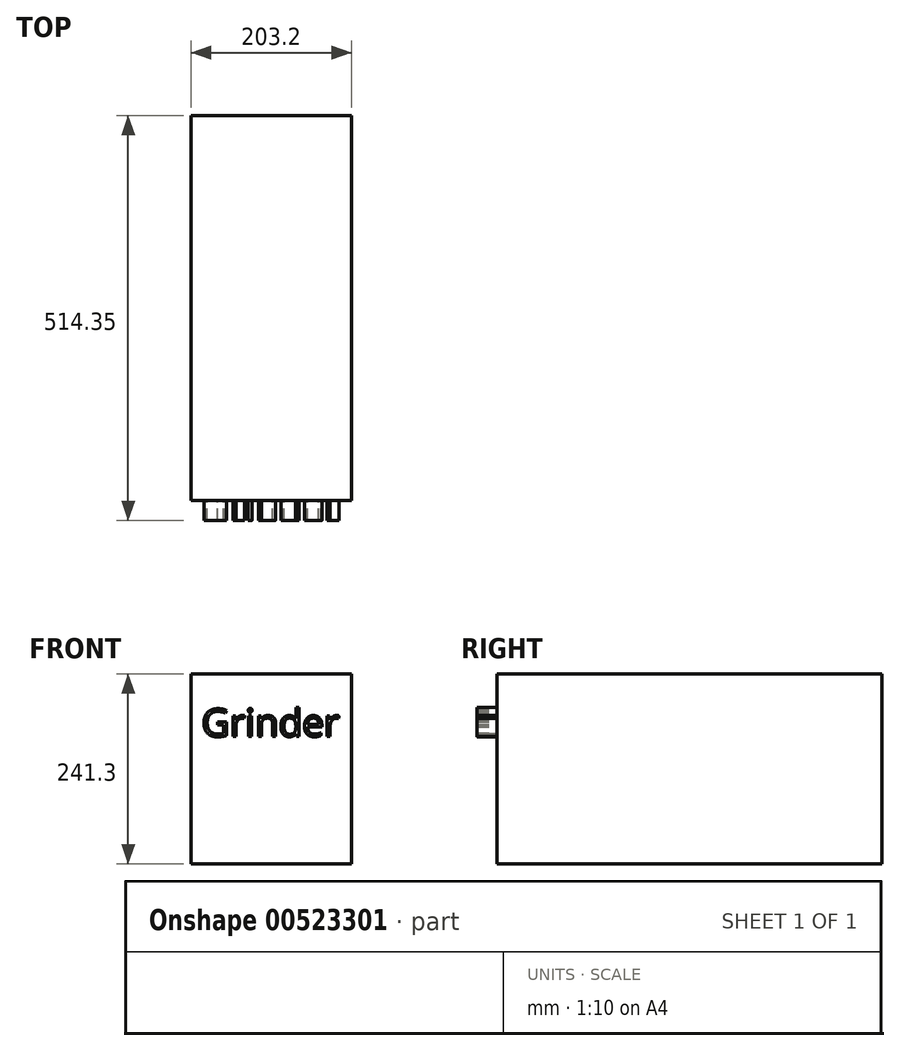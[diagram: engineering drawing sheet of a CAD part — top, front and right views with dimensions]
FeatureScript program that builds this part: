
annotation { "Feature Type Name" : "Feature", "Feature Type Description" : "" }
export const myFeature = defineFeature(function(context is Context, id is Id, definition is map)
    precondition{}
    {
        {
            var Q0;
            Q0=qCreatedBy(makeId("Front.planeOp"),FACE);
            var sketch = newSketch(context, id + "F0", { "sketchPlane" : qUnion([Q0])});
            skLineSegment(sketch, "E0.bottom", {"start": v(101.6, 120.65) * mm, "end": v(-101.6, 120.65) * mm});
            skLineSegment(sketch, "E0.top", {"start": v(101.6, -120.65) * mm, "end": v(-101.6, -120.65) * mm});
            skLineSegment(sketch, "E0.left", {"start": v(101.6, 120.65) * mm, "end": v(101.6, -120.65) * mm});
            skLineSegment(sketch, "E0.right", {"start": v(-101.6, 120.65) * mm, "end": v(-101.6, -120.65) * mm});
            skPoint(sketch, "E0.middle", {"position": v(0, 0) * mm});
            skSolve(sketch);
        }
        {
            var Q0;
            Q0=makeQuery(id+"F0.imprint","IMPRINT",FACE,{"disambiguationData":[TD([[makeQuery(id+"F0.imprint","IMPRINT",EDGE,{"derivedFrom":sQuery(id+"F0.wireOp",EDGE,"E0.bottom")}),1.0]])]});
            extrude(context, id + "F1", {"entities" : qUnion([Q0]), "depth" : 488.95 * mm, "offsetDistance" : 25.4 * mm});
        }
        {
            var Q0;
            Q0=makeQuery(id+"F1.opExtrude","CAP_FACE",FACE,{"disambiguationData":[OSD([sQuery(id+"F0.wireOp",EDGE,"E0.bottom"),sQuery(id+"F0.wireOp",EDGE,"E0.top"),sQuery(id+"F0.wireOp",EDGE,"E0.left"),sQuery(id+"F0.wireOp",EDGE,"E0.right")])],"isStart":false});
            var sketch = newSketch(context, id + "F2", { "sketchPlane" : qUnion([Q0])});
            skText(sketch, "E1", { "text": "Grinder", "fontName": "OpenSans-Regular.ttf"});
            const initialGuessF2  = {"E1": [-0.08862, 0.04125, 1, 0, 0.03521]};
            skSetInitialGuess(sketch, initialGuessF2);
            skSolve(sketch);
        }
        {
            var Q0;
            Q0 = qSketchRegion(id + "F2", true);
            extrude(context, id + "F3", {"entities" : qUnion([Q0]), "operationType" : NewBodyOperationType.ADD, "depth" : 25.4 * mm, "offsetDistance" : 25.4 * mm});
        }
    });
